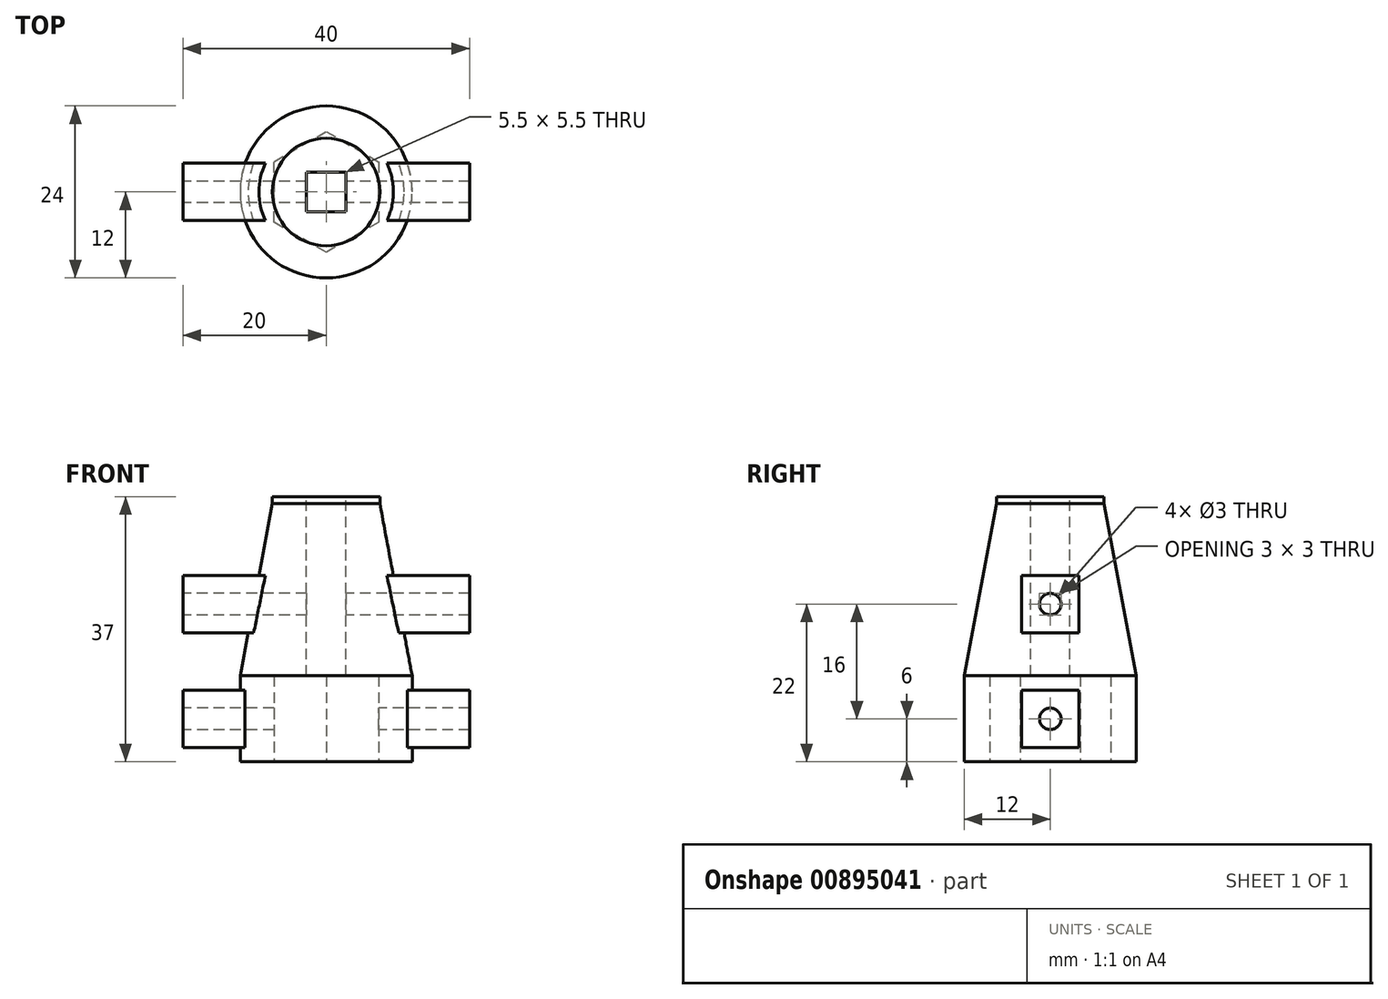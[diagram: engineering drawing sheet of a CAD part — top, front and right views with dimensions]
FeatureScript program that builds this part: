
annotation { "Feature Type Name" : "Feature", "Feature Type Description" : "" }
export const myFeature = defineFeature(function(context is Context, id is Id, definition is map)
    precondition{}
    {
        {
            var Q0;
            Q0=qCreatedBy(makeId("Top.planeOp"),FACE);
            var sketch = newSketch(context, id + "F0", { "sketchPlane" : qUnion([Q0])});
            skCircle(sketch, "E0.cCircle", {"center": v(0, 0) * mm, "radius": 7.3 * mm, "construction": true});
            skLineSegment(sketch, "E0.0", {"start": v(-7.3, 4.21) * mm, "end": v(0, 8.43) * mm});
            skLineSegment(sketch, "E0.1", {"start": v(0, 8.43) * mm, "end": v(7.3, 4.21) * mm});
            skLineSegment(sketch, "E0.2", {"start": v(7.3, 4.21) * mm, "end": v(7.3, -4.21) * mm});
            skLineSegment(sketch, "E0.3", {"start": v(7.3, -4.21) * mm, "end": v(0, -8.43) * mm});
            skLineSegment(sketch, "E0.4", {"start": v(0, -8.43) * mm, "end": v(-7.3, -4.21) * mm});
            skLineSegment(sketch, "E0.5", {"start": v(-7.3, -4.21) * mm, "end": v(-7.3, 4.21) * mm});
            skPoint(sketch, "E0.0.midPoint", {"position": v(-3.65, 6.32) * mm});
            skCircle(sketch, "E1", {"center": v(0, 0) * mm, "radius": 12 * mm});
            skSolve(sketch);
        }
        {
            var Q0;
            Q0=makeQuery(id+"F0.imprint","IMPRINT",FACE,{"disambiguationData":[TD([[makeQuery(id+"F0.imprint","IMPRINT",EDGE,{"derivedFrom":sQuery(id+"F0.wireOp",EDGE,"E0.0")}),1.0]])]});
            var Q1;
            Q1=makeQuery(id+"F0.imprint","IMPRINT",FACE,{"disambiguationData":[TD([[makeQuery(id+"F0.imprint","IMPRINT",EDGE,{"derivedFrom":sQuery(id+"F0.wireOp",EDGE,"E0.0")}),-1.0]])]});
            extrude(context, id + "F1", {"entities" : qUnion([Q0, Q1]), "depth" : 12 * mm, "offsetDistance" : 25 * mm});
        }
        {
            var Q0;
            Q0=makeQuery(id+"F1.opExtrude","CAP_FACE",FACE,{"disambiguationData":[OSD([sQuery(id+"F0.wireOp",EDGE,"E0.0"),sQuery(id+"F0.wireOp",EDGE,"E0.1"),sQuery(id+"F0.wireOp",EDGE,"E0.2"),sQuery(id+"F0.wireOp",EDGE,"E0.3"),sQuery(id+"F0.wireOp",EDGE,"E0.4"),sQuery(id+"F0.wireOp",EDGE,"E0.5"),sQuery(id+"F0.wireOp",EDGE,"E1")])],"isStart":false});
            cPlane(context, id + "F2", {"entities" : qUnion([Q0]), "cplaneType" : CPlaneType.OFFSET, "offset" : 25 * mm, "width" : 150 * mm, "height" : 150 * mm});
        }
        {
            var Q0;
            Q0=qCreatedBy(id+"F2.planeOp",FACE);
            var sketch = newSketch(context, id + "F3", { "sketchPlane" : qUnion([Q0])});
            skCircle(sketch, "E2", {"center": v(0, 0) * mm, "radius": 7.5 * mm});
            skLineSegment(sketch, "E3.bottom", {"start": v(2.75, 2.75) * mm, "end": v(-2.75, 2.75) * mm});
            skLineSegment(sketch, "E3.top", {"start": v(2.75, -2.75) * mm, "end": v(-2.75, -2.75) * mm});
            skLineSegment(sketch, "E3.left", {"start": v(2.75, 2.75) * mm, "end": v(2.75, -2.75) * mm});
            skLineSegment(sketch, "E3.right", {"start": v(-2.75, 2.75) * mm, "end": v(-2.75, -2.75) * mm});
            skSolve(sketch);
        }
        {
            var Q0;
            Q0=makeQuery(id+"F3.imprint","IMPRINT",FACE,{"disambiguationData":[TD([[makeQuery(id+"F3.imprint","IMPRINT",EDGE,{"derivedFrom":sQuery(id+"F3.wireOp",EDGE,"E2")}),1.0]])]});
            var Q1;
            Q1=makeQuery(id+"F3.imprint","IMPRINT",FACE,{"disambiguationData":[TD([[makeQuery(id+"F3.imprint","IMPRINT",EDGE,{"derivedFrom":sQuery(id+"F3.wireOp",EDGE,"E3.bottom")}),1.0]])]});
            extrude(context, id + "F4", {"entities" : qUnion([Q0, Q1]), "oppositeDirection" : true, "depth" : 1 * mm, "offsetDistance" : 25 * mm});
        }
        {
            var Q0;
            Q0=sQuery(id+"FVofQoZW4UbV0Pn_2.wireOp",EDGE,"0a6093ee-4388-4a00-bf8f-6446071e972f");
            var Q1;
            Q1=makeQuery(id+"F4.opExtrude","CAP_FACE",FACE,{"disambiguationData":[OSD([sQuery(id+"F3.wireOp",EDGE,"E2")])],"isStart":false});
            var Q2;
            Q2=makeQuery(id+"F1.opExtrude","CAP_FACE",FACE,{"disambiguationData":[OSD([sQuery(id+"F0.wireOp",EDGE,"E1")])],"isStart":false});
            loft(context, id + "F5", {"operationType" : NewBodyOperationType.ADD, "spine" : qUnion([Q0]), "sheetProfilesArray" : [{ "sheetProfileEntities" : qUnion([Q1]) }, { "sheetProfileEntities" : qUnion([Q2]) }]});
        }
        {
            var Q0;
            Q0=makeQuery(id+"F3.imprint","IMPRINT",FACE,{"disambiguationData":[TD([[makeQuery(id+"F3.imprint","IMPRINT",EDGE,{"derivedFrom":sQuery(id+"F3.wireOp",EDGE,"E3.bottom")}),1.0]])]});
            extrude(context, id + "F6", {"entities" : qUnion([Q0]), "operationType" : NewBodyOperationType.REMOVE, "oppositeDirection" : true, "depth" : 25 * mm, "offsetDistance" : 25 * mm});
        }
        {
            var Q0;
            Q0=makeQuery(id+"F0.imprint","IMPRINT",FACE,{"disambiguationData":[TD([[makeQuery(id+"F0.imprint","IMPRINT",EDGE,{"derivedFrom":sQuery(id+"F0.wireOp",EDGE,"E0.0")}),-1.0]])]});
            extrude(context, id + "F7", {"entities" : qUnion([Q0]), "operationType" : NewBodyOperationType.REMOVE, "depth" : 12 * mm, "offsetDistance" : 25 * mm});
        }
        {
            var Q0;
            Q0=qCreatedBy(makeId("Right.planeOp"),FACE);
            var sketch = newSketch(context, id + "F8", { "sketchPlane" : qUnion([Q0])});
            skCircle(sketch, "E4", {"center": v(0, 6) * mm, "radius": 1.5 * mm});
            skCircle(sketch, "E5", {"center": v(0, 22) * mm, "radius": 1.5 * mm});
            skLineSegment(sketch, "E6.bottom", {"start": v(4, 26) * mm, "end": v(-4, 26) * mm});
            skLineSegment(sketch, "E6.top", {"start": v(4, 18) * mm, "end": v(-4, 18) * mm});
            skLineSegment(sketch, "E6.left", {"start": v(4, 26) * mm, "end": v(4, 18) * mm});
            skLineSegment(sketch, "E6.right", {"start": v(-4, 26) * mm, "end": v(-4, 18) * mm});
            skLineSegment(sketch, "E7.bottom", {"start": v(4, 10) * mm, "end": v(-4, 10) * mm});
            skLineSegment(sketch, "E7.top", {"start": v(4, 2) * mm, "end": v(-4, 2) * mm});
            skLineSegment(sketch, "E7.left", {"start": v(4, 10) * mm, "end": v(4, 2) * mm});
            skLineSegment(sketch, "E7.right", {"start": v(-4, 10) * mm, "end": v(-4, 2) * mm});
            skSolve(sketch);
        }
        {
            var Q0;
            Q0 = qSketchRegion(id + "F8", true);
            extrude(context, id + "F9", {"entities" : qUnion([Q0]), "operationType" : NewBodyOperationType.ADD, "endBound" : BoundingType.SYMMETRIC, "depth" : 40 * mm, "offsetDistance" : 25 * mm});
        }
        {
            var Q0;
            Q0=makeQuery(id+"F9.boolean.opBoolean","SPLIT",FACE,{"disambiguationData":[TD([makeQuery(id+"F7.boolean.opBoolean","COPY",FACE,{"derivedFrom":makeQuery(id+"F7.opExtrude","SWEPT_FACE",FACE,{"disambiguationData":[OSD([sQuery(id+"F0.wireOp",EDGE,"E0.2")])]})})])],"derivedFrom":makeQuery(id+"F9.opExtrude","SWEPT_FACE",FACE,{"disambiguationData":[OSD([sQuery(id+"F8.wireOp",EDGE,"E7.top")])]})});
            extrude(context, id + "F10", {"entities" : qUnion([Q0]), "operationType" : NewBodyOperationType.REMOVE, "oppositeDirection" : true, "depth" : 8 * mm, "offsetDistance" : 25 * mm});
        }
        {
            var Q0;
            Q0=makeQuery(id+"F9.boolean.opBoolean","SPLIT",FACE,{"disambiguationData":[TD([makeQuery(id+"F6.boolean.opBoolean","COPY",FACE,{"derivedFrom":makeQuery(id+"F6.opExtrude","SWEPT_FACE",FACE,{"disambiguationData":[OSD([sQuery(id+"F3.wireOp",EDGE,"E3.bottom")])]})})])],"derivedFrom":makeQuery(id+"F9.opExtrude","SWEPT_FACE",FACE,{"disambiguationData":[OSD([sQuery(id+"F8.wireOp",EDGE,"E6.top")])]})});
            extrude(context, id + "F11", {"entities" : qUnion([Q0]), "operationType" : NewBodyOperationType.REMOVE, "oppositeDirection" : true, "depth" : 25 * mm, "offsetDistance" : 25 * mm});
        }
        {
            var Q0;
            Q0=makeQuery(id+"F8.imprint","IMPRINT",FACE,{"disambiguationData":[TD([[makeQuery(id+"F8.imprint","IMPRINT",EDGE,{"derivedFrom":sQuery(id+"F8.wireOp",EDGE,"E5")}),1.0]])]});
            var Q1;
            Q1=makeQuery(id+"F8.imprint","IMPRINT",FACE,{"disambiguationData":[TD([[makeQuery(id+"F8.imprint","IMPRINT",EDGE,{"derivedFrom":sQuery(id+"F8.wireOp",EDGE,"E4")}),1.0]])]});
            extrude(context, id + "F12", {"entities" : qUnion([Q0, Q1]), "operationType" : NewBodyOperationType.REMOVE, "endBound" : BoundingType.SYMMETRIC, "oppositeDirection" : true, "depth" : 25 * mm, "offsetDistance" : 25 * mm});
        }
    });
